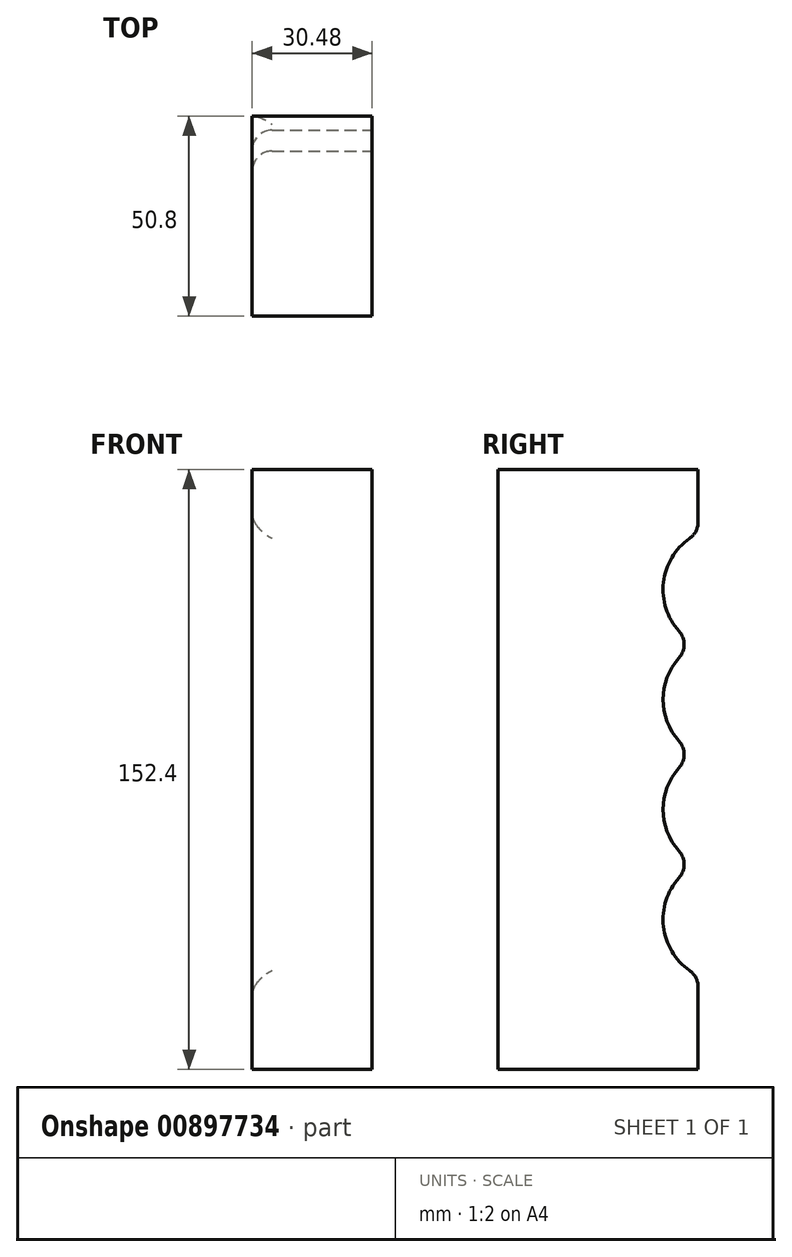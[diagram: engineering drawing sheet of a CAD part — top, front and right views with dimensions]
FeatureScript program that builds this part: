
annotation { "Feature Type Name" : "Feature", "Feature Type Description" : "" }
export const myFeature = defineFeature(function(context is Context, id is Id, definition is map)
    precondition{}
    {
        {
            var Q0;
            Q0=qCreatedBy(makeId("Front.planeOp"),FACE);
            var sketch = newSketch(context, id + "F0", { "sketchPlane" : qUnion([Q0])});
            skLineSegment(sketch, "E0.bottom", {"start": v(-14.99, 0) * mm, "end": v(15.5, 0) * mm});
            skLineSegment(sketch, "E0.top", {"start": v(-14.99, 152.4) * mm, "end": v(15.5, 152.4) * mm});
            skLineSegment(sketch, "E0.left", {"start": v(-14.99, 0) * mm, "end": v(-14.99, 152.4) * mm});
            skLineSegment(sketch, "E0.right", {"start": v(15.5, 0) * mm, "end": v(15.5, 152.4) * mm});
            skSolve(sketch);
        }
        {
            var Q0;
            Q0 = qSketchRegion(id + "F0", true);
            extrude(context, id + "F1", {"entities" : qUnion([Q0]), "oppositeDirection" : true, "depth" : 50.8 * mm, "offsetDistance" : 25.4 * mm});
        }
        {
            var Q0;
            Q0=makeQuery(id+"F1.opExtrude","SWEPT_FACE",FACE,{"disambiguationData":[OSD([sQuery(id+"F0.wireOp",EDGE,"E0.right")])]});
            var sketch = newSketch(context, id + "F2", { "sketchPlane" : qUnion([Q0])});
            skPoint(sketch, "E1.midSnap0", {"position": v(50.8, 76.2) * mm});
            skCircle(sketch, "E2", {"center": v(57.78, 121.92) * mm, "radius": 15.88 * mm});
            skLineSegment(sketch, "E3", {"start": v(57.78, 121.92) * mm, "end": v(57.79, 0) * mm, "construction": true});
            skCircle(sketch, "E4", {"center": v(57.78, 93.98) * mm, "radius": 15.88 * mm});
            skCircle(sketch, "E5", {"center": v(57.79, 66.04) * mm, "radius": 15.88 * mm});
            skCircle(sketch, "E6", {"center": v(57.79, 38.1) * mm, "radius": 15.88 * mm});
            skSolve(sketch);
        }
        {
            var Q0;
            Q0 = qSketchRegion(id + "F2", true);
            extrude(context, id + "F3", {"entities" : qUnion([Q0]), "operationType" : NewBodyOperationType.REMOVE, "endBound" : BoundingType.THROUGH_ALL, "oppositeDirection" : true, "depth" : 25.4 * mm, "offsetDistance" : 25.4 * mm});
        }
        {
            var Q0;
            Q0=makeQuery(id+"F3.boolean.opBoolean","COPY",EDGE,{"derivedFrom":makeQuery(id+"F3.opExtrude","CAP_EDGE",EDGE,{"disambiguationData":[OSD([sQuery(id+"F2.wireOp",EDGE,"E2")])],"isStart":true})});
            var Q1;
            {var subQ0=sQuery(id+"F2.wireOp",EDGE,"E4");Q1=makeQuery(id+"F3.boolean.opBoolean","COPY",EDGE,{"derivedFrom":makeQuery(id+"F3.opExtrude","CAP_EDGE",EDGE,{"disambiguationData":[OSD([subQ0]),TDD([makeQuery(id+"F2.imprint","IMPRINT",EDGE,{"disambiguationData":[TD([[makeQuery(id+"F2.imprint","INTERSECT",VERTEX,{"disambiguationData":[OD(1.0)],"derivedFrom":[sQuery(id+"F2.wireOp",EDGE,"E2"),subQ0]}),-1.0]])],"derivedFrom":subQ0})])],"isStart":true})});}
            var Q2;
            {var subQ0=sQuery(id+"F2.wireOp",EDGE,"E5");Q2=makeQuery(id+"F3.boolean.opBoolean","COPY",EDGE,{"derivedFrom":makeQuery(id+"F3.opExtrude","CAP_EDGE",EDGE,{"disambiguationData":[OSD([subQ0]),TDD([makeQuery(id+"F2.imprint","IMPRINT",EDGE,{"disambiguationData":[TD([[makeQuery(id+"F2.imprint","INTERSECT",VERTEX,{"disambiguationData":[OD(1.0)],"derivedFrom":[sQuery(id+"F2.wireOp",EDGE,"E4"),subQ0]}),-1.0]])],"derivedFrom":subQ0})])],"isStart":true})});}
            var Q3;
            Q3=makeQuery(id+"F3.boolean.opBoolean","COPY",EDGE,{"derivedFrom":makeQuery(id+"F3.opExtrude","CAP_EDGE",EDGE,{"disambiguationData":[OSD([sQuery(id+"F2.wireOp",EDGE,"E6")])],"isStart":true})});
            var Q4;
            Q4=makeQuery(id+"F3.boolean.opBoolean","INTERSECT",EDGE,{"derivedFrom":[makeQuery(id+"F1.opExtrude","SWEPT_FACE",FACE,{"disambiguationData":[OSD([sQuery(id+"F0.wireOp",EDGE,"E0.left")])]}),makeQuery(id+"F3.opExtrude","SWEPT_FACE",FACE,{"disambiguationData":[OSD([sQuery(id+"F2.wireOp",EDGE,"E2")])]})]});
            var Q5;
            {var subQ0=sQuery(id+"F2.wireOp",EDGE,"E4");Q5=makeQuery(id+"F3.boolean.opBoolean","INTERSECT",EDGE,{"derivedFrom":[makeQuery(id+"F1.opExtrude","SWEPT_FACE",FACE,{"disambiguationData":[OSD([sQuery(id+"F0.wireOp",EDGE,"E0.left")])]}),makeQuery(id+"F3.opExtrude","SWEPT_FACE",FACE,{"disambiguationData":[OSD([subQ0]),TDD([makeQuery(id+"F2.imprint","IMPRINT",EDGE,{"disambiguationData":[TD([[makeQuery(id+"F2.imprint","INTERSECT",VERTEX,{"disambiguationData":[OD(1.0)],"derivedFrom":[sQuery(id+"F2.wireOp",EDGE,"E2"),subQ0]}),-1.0]])],"derivedFrom":subQ0})])]})]});}
            var Q6;
            {var subQ0=sQuery(id+"F2.wireOp",EDGE,"E5");Q6=makeQuery(id+"F3.boolean.opBoolean","INTERSECT",EDGE,{"derivedFrom":[makeQuery(id+"F1.opExtrude","SWEPT_FACE",FACE,{"disambiguationData":[OSD([sQuery(id+"F0.wireOp",EDGE,"E0.left")])]}),makeQuery(id+"F3.opExtrude","SWEPT_FACE",FACE,{"disambiguationData":[OSD([subQ0]),TDD([makeQuery(id+"F2.imprint","IMPRINT",EDGE,{"disambiguationData":[TD([[makeQuery(id+"F2.imprint","INTERSECT",VERTEX,{"disambiguationData":[OD(1.0)],"derivedFrom":[sQuery(id+"F2.wireOp",EDGE,"E4"),subQ0]}),-1.0]])],"derivedFrom":subQ0})])]})]});}
            var Q7;
            Q7=makeQuery(id+"F3.boolean.opBoolean","INTERSECT",EDGE,{"derivedFrom":[makeQuery(id+"F1.opExtrude","SWEPT_FACE",FACE,{"disambiguationData":[OSD([sQuery(id+"F0.wireOp",EDGE,"E0.left")])]}),makeQuery(id+"F3.opExtrude","SWEPT_FACE",FACE,{"disambiguationData":[OSD([sQuery(id+"F2.wireOp",EDGE,"E6")])]})]});
            var Q8;
            Q8=makeQuery(id+"F3.boolean.opBoolean","INTERSECT",EDGE,{"derivedFrom":[makeQuery(id+"F1.opExtrude","CAP_FACE",FACE,{"disambiguationData":[OSD([sQuery(id+"F0.wireOp",EDGE,"E0.bottom"),sQuery(id+"F0.wireOp",EDGE,"E0.top"),sQuery(id+"F0.wireOp",EDGE,"E0.left"),sQuery(id+"F0.wireOp",EDGE,"E0.right")])],"isStart":false}),makeQuery(id+"F3.opExtrude","SWEPT_FACE",FACE,{"disambiguationData":[OSD([sQuery(id+"F2.wireOp",EDGE,"E6")])]})]});
            var Q9;
            {var subQ0=sQuery(id+"F2.wireOp",EDGE,"E6");var subQ1=sQuery(id+"F2.wireOp",EDGE,"E5");Q9=makeQuery(id+"F3.boolean.opBoolean","COPY",EDGE,{"derivedFrom":makeQuery(id+"F3.opExtrude","SWEPT_EDGE",EDGE,{"disambiguationData":[OSD([subQ1,subQ0]),TDD([makeQuery(id+"F2.imprint","INTERSECT",VERTEX,{"disambiguationData":[OD(1.0)],"derivedFrom":[subQ1,subQ0]})])]})});}
            var Q10;
            {var subQ0=sQuery(id+"F2.wireOp",EDGE,"E5");var subQ1=sQuery(id+"F2.wireOp",EDGE,"E4");Q10=makeQuery(id+"F3.boolean.opBoolean","COPY",EDGE,{"derivedFrom":makeQuery(id+"F3.opExtrude","SWEPT_EDGE",EDGE,{"disambiguationData":[OSD([subQ1,subQ0]),TDD([makeQuery(id+"F2.imprint","INTERSECT",VERTEX,{"disambiguationData":[OD(1.0)],"derivedFrom":[subQ1,subQ0]})])]})});}
            var Q11;
            {var subQ0=sQuery(id+"F2.wireOp",EDGE,"E4");var subQ1=sQuery(id+"F2.wireOp",EDGE,"E2");Q11=makeQuery(id+"F3.boolean.opBoolean","COPY",EDGE,{"derivedFrom":makeQuery(id+"F3.opExtrude","SWEPT_EDGE",EDGE,{"disambiguationData":[OSD([subQ1,subQ0]),TDD([makeQuery(id+"F2.imprint","INTERSECT",VERTEX,{"disambiguationData":[OD(1.0)],"derivedFrom":[subQ1,subQ0]})])]})});}
            var Q12;
            Q12=makeQuery(id+"F3.boolean.opBoolean","INTERSECT",EDGE,{"derivedFrom":[makeQuery(id+"F1.opExtrude","CAP_FACE",FACE,{"disambiguationData":[OSD([sQuery(id+"F0.wireOp",EDGE,"E0.bottom"),sQuery(id+"F0.wireOp",EDGE,"E0.top"),sQuery(id+"F0.wireOp",EDGE,"E0.left"),sQuery(id+"F0.wireOp",EDGE,"E0.right")])],"isStart":false}),makeQuery(id+"F3.opExtrude","SWEPT_FACE",FACE,{"disambiguationData":[OSD([sQuery(id+"F2.wireOp",EDGE,"E2")])]})]});
            fillet(context, id + "F4", {"entities" : qUnion([Q0, Q1, Q2, Q3, Q4, Q5, Q6, Q7, Q8, Q9, Q10, Q11, Q12]), "radius" : 5.08 * mm, "tangentPropagation" : true, "allowEdgeOverflow" : false});
        }
    });
